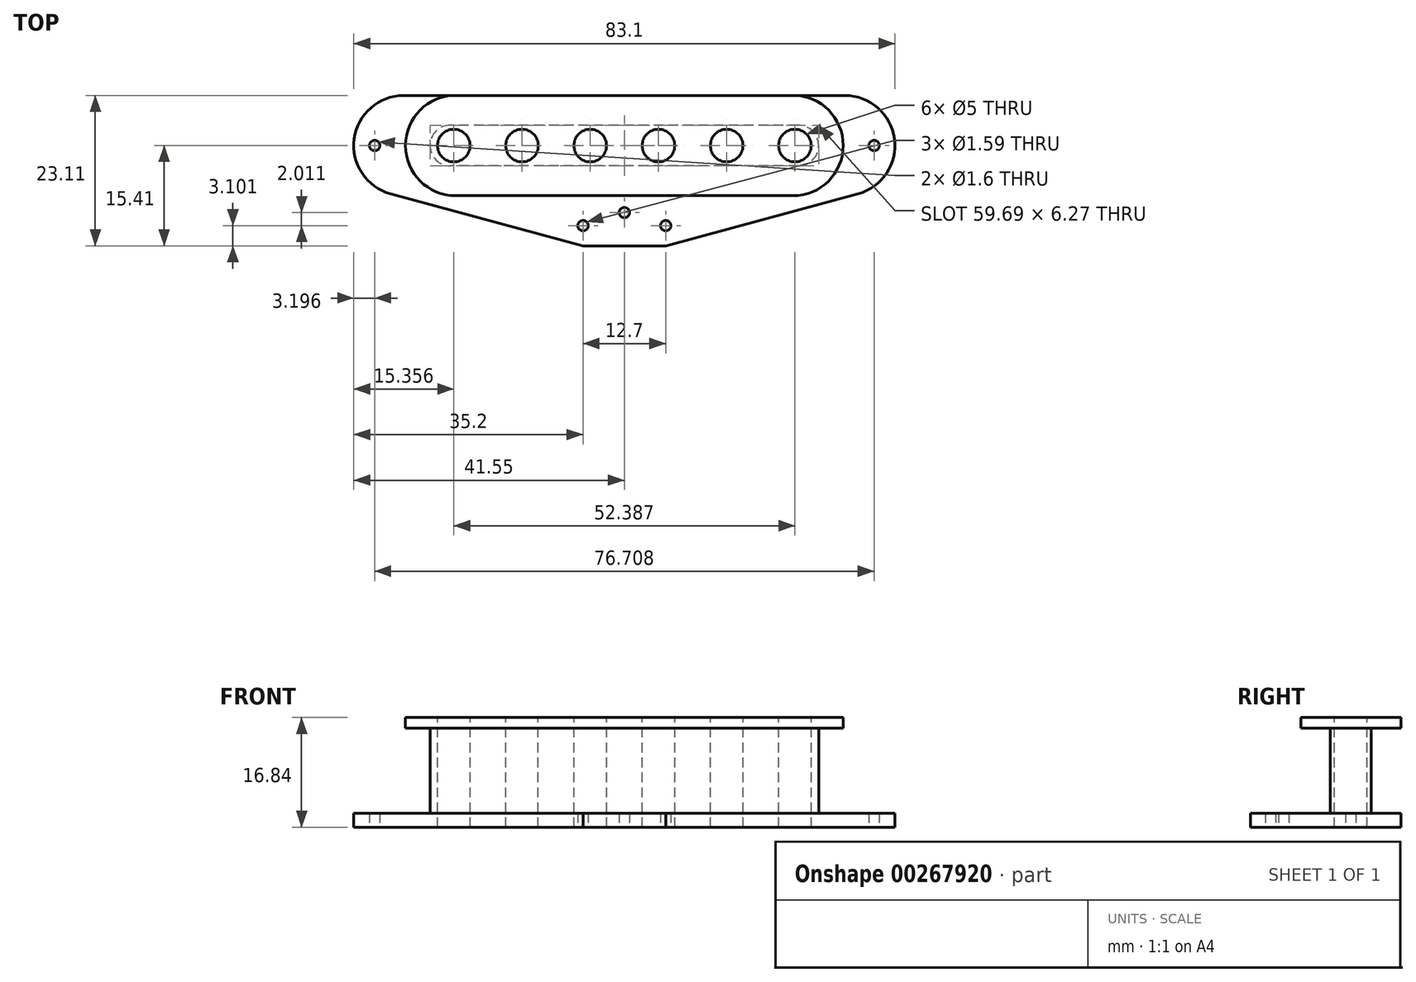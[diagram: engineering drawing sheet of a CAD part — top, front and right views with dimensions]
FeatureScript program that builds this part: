
annotation { "Feature Type Name" : "Feature", "Feature Type Description" : "" }
export const myFeature = defineFeature(function(context is Context, id is Id, definition is map)
    precondition{}
    {
        {
            var Q0;
            Q0=qCreatedBy(makeId("Top.planeOp"),FACE);
            var sketch = newSketch(context, id + "F0", { "sketchPlane" : qUnion([Q0])});
            skLineSegment(sketch, "E0", {"start": v(-1.43, 7.7) * mm, "end": v(25.92, 7.7) * mm});
            skLineSegment(sketch, "E1.MirrorCS", {"start": v(1.43, 7.7) * mm, "end": v(-25.92, 7.7) * mm});
            skLineSegment(sketch, "E2.MirrorCS", {"start": v(-1.43, -7.7) * mm, "end": v(25.92, -7.7) * mm});
            skLineSegment(sketch, "E3.MirrorCS", {"start": v(1.43, -7.7) * mm, "end": v(-25.92, -7.7) * mm});
            skArc(sketch, "E4", {"start": v(25.92, -7.7) * mm, "mid": v(33.62, 0) * mm, "end": v(25.92, 7.7) * mm});
            skArc(sketch, "E5.MirrorCS", {"start": v(-25.92, -7.7) * mm, "mid": v(-33.62, 0) * mm, "end": v(-25.92, 7.7) * mm});
            skLineSegment(sketch, "E6", {"start": v(0, 0) * mm, "end": v(33.62, 0) * mm, "construction": true});
            skLineSegment(sketch, "E7", {"start": v(25.92, 7.7) * mm, "end": v(25.92, -7.7) * mm, "construction": true});
            skSolve(sketch);
        }
        {
            var Q0;
            Q0 = qSketchRegion(id + "F0", true);
            extrude(context, id + "F1", {"entities" : qUnion([Q0]), "depth" : 1.6 * mm});
        }
        {
            var Q0;
            Q0=qCreatedBy(makeId("Top.planeOp"),FACE);
            cPlane(context, id + "F2", {"entities" : qUnion([Q0]), "cplaneType" : CPlaneType.OFFSET, "offset" : 13.08 * mm, "oppositeDirection" : true, "width" : 152.4 * mm, "height" : 152.4 * mm});
        }
        {
            var Q0;
            Q0=qCreatedBy(id+"F2.planeOp",FACE);
            var sketch = newSketch(context, id + "F3", { "sketchPlane" : qUnion([Q0])});
            skLineSegment(sketch, "E8", {"start": v(0, 0) * mm, "end": v(41.55, 0) * mm, "construction": true});
            skLineSegment(sketch, "E9.0", {"start": v(-6.35, -15.4) * mm, "end": v(6.35, -15.4) * mm});
            skPoint(sketch, "E10.orphan", {"position": v(-77.67, 0) * mm});
            skLineSegment(sketch, "E11", {"start": v(0, 7.7) * mm, "end": v(33.86, 7.7) * mm});
            skArc(sketch, "E12", {"start": v(35.87, -7.43) * mm, "mid": v(41.49, 1.01) * mm, "end": v(33.86, 7.7) * mm});
            skLineSegment(sketch, "E13.MirrorCS", {"start": v(0, 7.7) * mm, "end": v(-33.86, 7.7) * mm});
            skArc(sketch, "E14.MirrorCS", {"start": v(-35.87, -7.43) * mm, "mid": v(-41.49, 1.01) * mm, "end": v(-33.86, 7.7) * mm});
            skLineSegment(sketch, "E15", {"start": v(6.35, -15.4) * mm, "end": v(35.87, -7.43) * mm});
            skLineSegment(sketch, "E16", {"start": v(-6.35, -15.4) * mm, "end": v(-35.87, -7.43) * mm});
            skSolve(sketch);
        }
        {
            var Q0;
            Q0 = qSketchRegion(id + "F3", true);
            extrude(context, id + "F4", {"entities" : qUnion([Q0]), "oppositeDirection" : true, "depth" : 2.16 * mm});
        }
        {
            var Q0;
            Q0=makeQuery(id+"F1.opExtrude","CAP_FACE",FACE,{"disambiguationData":[OSD([sQuery(id+"F0.wireOp",EDGE,"E0"),sQuery(id+"F0.wireOp",EDGE,"E1.MirrorCS"),sQuery(id+"F0.wireOp",EDGE,"E2.MirrorCS"),sQuery(id+"F0.wireOp",EDGE,"E3.MirrorCS"),sQuery(id+"F0.wireOp",EDGE,"E4"),sQuery(id+"F0.wireOp",EDGE,"E5.MirrorCS")])],"isStart":true});
            var sketch = newSketch(context, id + "F5", { "sketchPlane" : qUnion([Q0])});
            skLineSegment(sketch, "E17", {"start": v(0, 0) * mm, "end": v(0, 11.98) * mm, "construction": true});
            skLineSegment(sketch, "E18", {"start": v(0, 0) * mm, "end": v(26.7, 0) * mm, "construction": true});
            skPoint(sketch, "E18.endSnap0", {"position": v(33.62, 0) * mm});
            skArc(sketch, "E19", {"start": v(26.7, -3.14) * mm, "mid": v(29.85, 0) * mm, "end": v(26.7, 3.14) * mm});
            skLineSegment(sketch, "E20", {"start": v(26.7, 3.14) * mm, "end": v(0, 3.14) * mm});
            skLineSegment(sketch, "E21.MirrorCS", {"start": v(26.7, -3.14) * mm, "end": v(0, -3.14) * mm});
            skLineSegment(sketch, "E22.MirrorCS", {"start": v(-26.7, -3.14) * mm, "end": v(0, -3.14) * mm});
            skArc(sketch, "E23.MirrorCS", {"start": v(-26.7, -3.14) * mm, "mid": v(-29.85, 0) * mm, "end": v(-26.7, 3.14) * mm});
            skLineSegment(sketch, "E24.MirrorCS", {"start": v(-26.7, 3.14) * mm, "end": v(0, 3.14) * mm});
            skSolve(sketch);
        }
        {
            var Q0;
            Q0 = qSketchRegion(id + "F5", true);
            extrude(context, id + "F6", {"entities" : qUnion([Q0]), "operationType" : NewBodyOperationType.ADD, "endBound" : BoundingType.UP_TO_NEXT, "depth" : 12.7 * mm});
        }
        {
            var Q0;
            Q0=makeQuery(id+"F1.opExtrude","CAP_FACE",FACE,{"disambiguationData":[OSD([sQuery(id+"F0.wireOp",EDGE,"E0"),sQuery(id+"F0.wireOp",EDGE,"E1.MirrorCS"),sQuery(id+"F0.wireOp",EDGE,"E2.MirrorCS"),sQuery(id+"F0.wireOp",EDGE,"E3.MirrorCS"),sQuery(id+"F0.wireOp",EDGE,"E4"),sQuery(id+"F0.wireOp",EDGE,"E5.MirrorCS")])],"isStart":false});
            var sketch = newSketch(context, id + "F7", { "sketchPlane" : qUnion([Q0])});
            skLineSegment(sketch, "E25", {"start": v(0, 0) * mm, "end": v(0, -5.62) * mm, "construction": true});
            skPoint(sketch, "E25.endSnap0", {"position": v(0, -7.7) * mm});
            skCircle(sketch, "E26", {"center": v(-5.24, 0) * mm, "radius": 2.5 * mm});
            skCircle(sketch, "E27.1.0.0", {"center": v(-15.72, 0) * mm, "radius": 2.5 * mm});
            skCircle(sketch, "E27.2.0.0", {"center": v(-26.2, 0) * mm, "radius": 2.5 * mm});
            skLineSegment(sketch, "E27.direction1", {"start": v(-5.24, 0) * mm, "end": v(-15.72, 0) * mm, "construction": true});
            skCircle(sketch, "E28.MirrorC", {"center": v(5.24, 0) * mm, "radius": 2.5 * mm});
            skCircle(sketch, "E29.MirrorC", {"center": v(15.72, 0) * mm, "radius": 2.5 * mm});
            skCircle(sketch, "E30.MirrorC", {"center": v(26.2, 0) * mm, "radius": 2.5 * mm});
            skSolve(sketch);
        }
        {
            var Q0;
            Q0 = qSketchRegion(id + "F7", true);
            extrude(context, id + "F8", {"entities" : qUnion([Q0]), "operationType" : NewBodyOperationType.REMOVE, "endBound" : BoundingType.THROUGH_ALL, "oppositeDirection" : true, "depth" : 25.4 * mm});
        }
        {
            var Q0;
            Q0=makeQuery(id+"F4.opExtrude","CAP_FACE",FACE,{"disambiguationData":[OSD([sQuery(id+"F3.wireOp",EDGE,"E9.0"),sQuery(id+"F3.wireOp",EDGE,"E11"),sQuery(id+"F3.wireOp",EDGE,"E12"),sQuery(id+"F3.wireOp",EDGE,"E13.MirrorCS"),sQuery(id+"F3.wireOp",EDGE,"E14.MirrorCS"),sQuery(id+"F3.wireOp",EDGE,"E15"),sQuery(id+"F3.wireOp",EDGE,"E16")])],"isStart":false});
            var sketch = newSketch(context, id + "F9", { "sketchPlane" : qUnion([Q0])});
            skLineSegment(sketch, "E31", {"start": v(0, 0) * mm, "end": v(38.35, 0) * mm, "construction": true});
            skCircle(sketch, "E32", {"center": v(38.35, 0) * mm, "radius": 0.8 * mm});
            skLineSegment(sketch, "E33", {"start": v(0, 0) * mm, "end": v(0, 18.79) * mm, "construction": true});
            skCircle(sketch, "E34.MirrorC", {"center": v(-38.35, 0) * mm, "radius": 0.8 * mm});
            skCircle(sketch, "E35", {"center": v(-6.35, 12.3) * mm, "radius": 0.8 * mm});
            skCircle(sketch, "E36", {"center": v(0, 10.3) * mm, "radius": 0.8 * mm});
            skCircle(sketch, "E37.MirrorC", {"center": v(6.35, 12.3) * mm, "radius": 0.8 * mm});
            skSolve(sketch);
        }
        {
            var Q0;
            Q0 = qSketchRegion(id + "F9", true);
            extrude(context, id + "F10", {"entities" : qUnion([Q0]), "operationType" : NewBodyOperationType.REMOVE, "endBound" : BoundingType.THROUGH_ALL, "oppositeDirection" : true, "depth" : 25.4 * mm});
        }
    });
